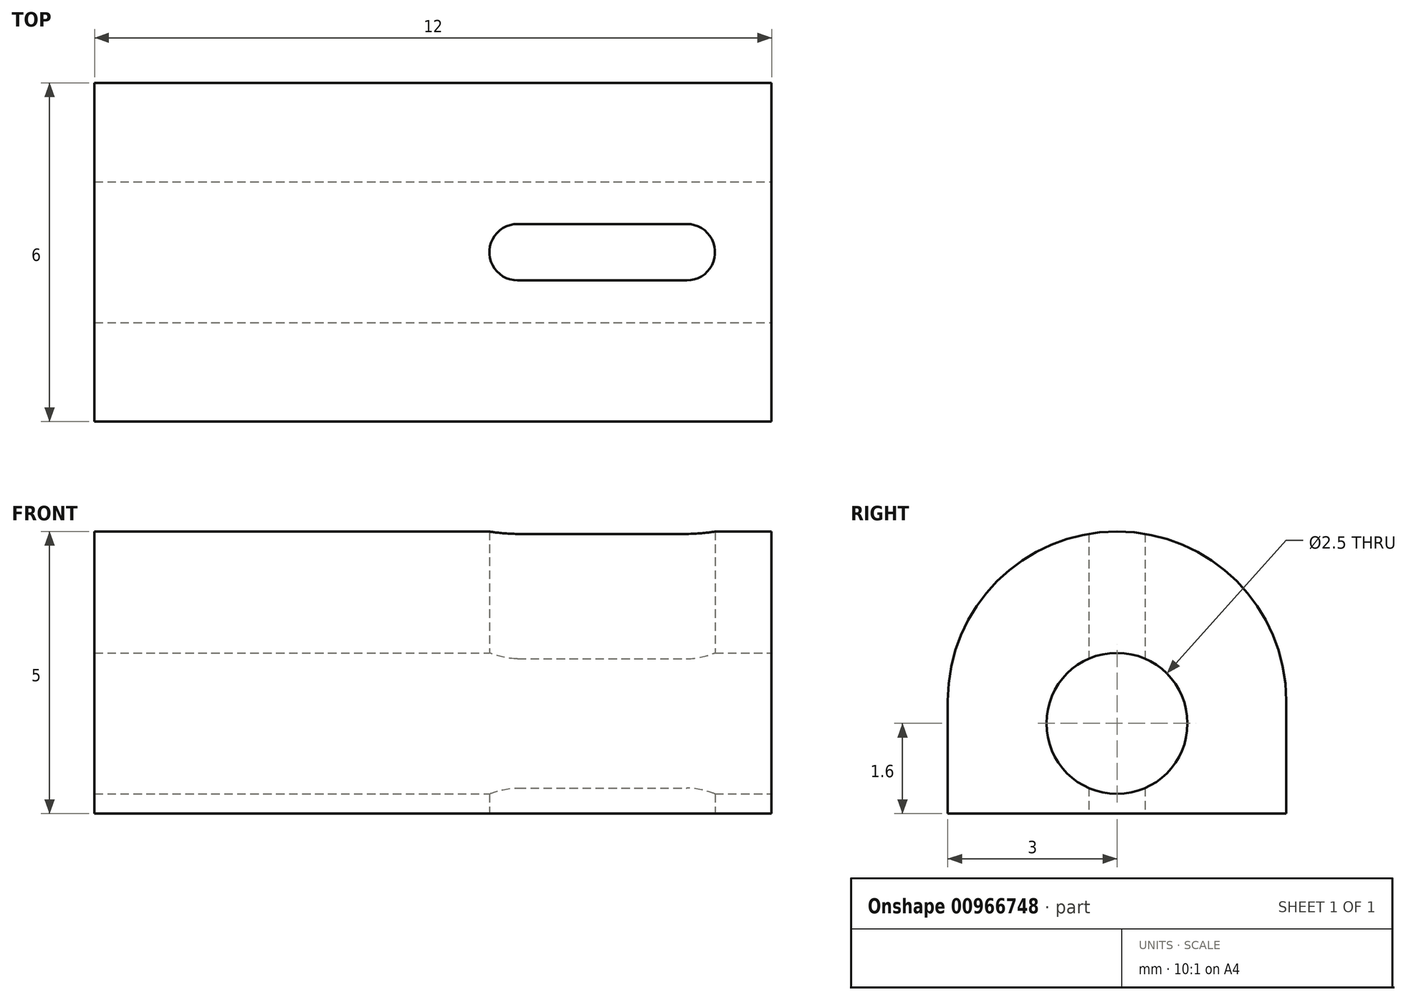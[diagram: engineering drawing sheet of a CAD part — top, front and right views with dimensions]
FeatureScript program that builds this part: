
annotation { "Feature Type Name" : "Feature", "Feature Type Description" : "" }
export const myFeature = defineFeature(function(context is Context, id is Id, definition is map)
    precondition{}
    {
        {
            var Q0;
            Q0=qCreatedBy(makeId("Top.planeOp"),FACE);
            var sketch = newSketch(context, id + "F0", { "sketchPlane" : qUnion([Q0])});
            skLineSegment(sketch, "E0.bottom", {"start": v(6.46, 3) * mm, "end": v(18.46, 3) * mm});
            skLineSegment(sketch, "E0.top", {"start": v(6.46, -3) * mm, "end": v(18.46, -3) * mm});
            skLineSegment(sketch, "E0.left", {"start": v(6.46, 3) * mm, "end": v(6.46, -3) * mm});
            skLineSegment(sketch, "E0.right", {"start": v(18.46, 3) * mm, "end": v(18.46, -3) * mm});
            skSolve(sketch);
        }
        {
            var Q0;
            Q0=makeQuery(id+"F0.imprint","IMPRINT",FACE,{"disambiguationData":[TD([[makeQuery(id+"F0.imprint","IMPRINT",EDGE,{"derivedFrom":sQuery(id+"F0.wireOp",EDGE,"E0.bottom")}),-1.0]])]});
            extrude(context, id + "F1", {"entities" : qUnion([Q0]), "depth" : 5 * mm, "offsetDistance" : 25 * mm});
        }
        {
            var Q0;
            Q0=makeQuery(id+"F1.opExtrude","CAP_EDGE",EDGE,{"disambiguationData":[OSD([sQuery(id+"F0.wireOp",EDGE,"E0.top")])],"isStart":false});
            var Q1;
            Q1=makeQuery(id+"F1.opExtrude","CAP_EDGE",EDGE,{"disambiguationData":[OSD([sQuery(id+"F0.wireOp",EDGE,"E0.bottom")])],"isStart":false});
            fillet(context, id + "F2", {"entities" : qUnion([Q0, Q1]), "radius" : 3 * mm, "tangentPropagation" : true, "allowEdgeOverflow" : false});
        }
        {
            var Q0;
            Q0=makeQuery(id+"F1.opExtrude","SWEPT_FACE",FACE,{"disambiguationData":[OSD([sQuery(id+"F0.wireOp",EDGE,"E0.right")])]});
            var sketch = newSketch(context, id + "F3", { "sketchPlane" : qUnion([Q0])});
            skCircle(sketch, "E1", {"center": v(0, 1.6) * mm, "radius": 1.25 * mm});
            skSolve(sketch);
        }
        {
            var Q0;
            Q0=makeQuery(id+"F3.imprint","IMPRINT",FACE,{"disambiguationData":[TD([[makeQuery(id+"F3.imprint","IMPRINT",EDGE,{"derivedFrom":sQuery(id+"F3.wireOp",EDGE,"E1")}),1.0]])]});
            extrude(context, id + "F4", {"entities" : qUnion([Q0]), "operationType" : NewBodyOperationType.REMOVE, "oppositeDirection" : true, "depth" : 25 * mm, "offsetDistance" : 25 * mm});
        }
        {
            var Q0;
            Q0=makeQuery(id+"F1.opExtrude","CAP_FACE",FACE,{"disambiguationData":[OSD([sQuery(id+"F0.wireOp",EDGE,"E0.bottom"),sQuery(id+"F0.wireOp",EDGE,"E0.top"),sQuery(id+"F0.wireOp",EDGE,"E0.left"),sQuery(id+"F0.wireOp",EDGE,"E0.right")])],"isStart":true});
            var sketch = newSketch(context, id + "F5", { "sketchPlane" : qUnion([Q0])});
            skArc(sketch, "E2", {"start": v(16.96, -0.5) * mm, "mid": v(17.46, 0) * mm, "end": v(16.96, 0.5) * mm});
            skArc(sketch, "E3", {"start": v(13.96, 0.5) * mm, "mid": v(13.46, 0) * mm, "end": v(13.96, -0.5) * mm});
            skLineSegment(sketch, "E4", {"start": v(13.96, 0.5) * mm, "end": v(16.96, 0.5) * mm});
            skLineSegment(sketch, "E5.MirrorCS", {"start": v(13.96, -0.5) * mm, "end": v(16.96, -0.5) * mm});
            skSolve(sketch);
        }
        {
            var Q0;
            Q0=makeQuery(id+"F5.imprint","IMPRINT",FACE,{"disambiguationData":[TD([[makeQuery(id+"F5.imprint","IMPRINT",EDGE,{"derivedFrom":sQuery(id+"F5.wireOp",EDGE,"E2")}),1.0]])]});
            extrude(context, id + "F6", {"entities" : qUnion([Q0]), "operationType" : NewBodyOperationType.REMOVE, "oppositeDirection" : true, "depth" : 25 * mm, "offsetDistance" : 25 * mm});
        }
    });
